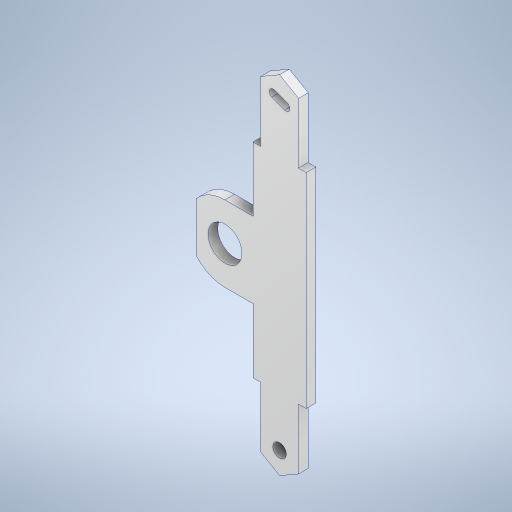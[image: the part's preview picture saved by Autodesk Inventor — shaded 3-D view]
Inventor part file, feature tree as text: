
AUTODESK INVENTOR PART (.ipt)
format: ipt  version: 2024 (Build 280153000, 153)  size: 352,256 bytes
history: native  units: mm
features: sketch x4, extrude x2, mirror x2, hole x2, fillet x2, projected_geometry x2
ambient origin geometry x8: Origin, YZ Plane, XZ Plane, XY Plane, X Axis, Y Axis, Z Axis, Center Point
bodies: Solid1 (feature_tree)
feature tree (14):
  extrude  "Extrusion1"  Depth=25.0mm
  extrude  "Extrusion2"  Depth=5.3mm
  mirror  "Mirror1"
  mirror  "Mirror2"
  hole  "Hole1"  [1 undecoded]
  hole  "Hole2"  [1 undecoded]
  fillet  "Fillet2"  Radius=42.0mm
  fillet  "Fillet3"  Radius=30.0mm
  sketch  "Sketch1"  dims[d0=25.0mm d1=266.0mm]
  sketch  "Sketch2"  dims[d2=200.0mm d3=5.3mm]
  projected_geometry  "Projected Loop1"
  sketch  "Sketch3"  dims[d4=9.0mm d5=9.0mm]
  projected_geometry  "Projected Loop2"
  sketch  "Sketch4"  dims[d6=22.4mm d7=36.0mm d8=42.0mm d9=30.0mm d10=4.0mm d11=4.0mm d12=134.75mm d13=35.0mm d14=6.35mm d15=0.0mm d16=0.75mm d17=2.75mm d18=0.75mm d19=0.0mm d20=0.0mm d21=32.0mm d22=45.0deg d23=3.242mm d24=8.0mm d25=4.0mm d26=2.0mm d27=90.0deg d28=8.0mm d29=20.594885mm d30=20.0mm d32=10.0mm d33=5.3mm d34=8.0mm d35=4.0mm d36=2.0mm d37=90.0deg d38=8.0mm d39=20.594885mm d41=3.0mm d42=1.0mm]
note: 2 required parameter values undecoded (feature->parameter linkage not recoverable at this tier; creation-order binding heuristic only, values carry confidence <= 0.55)
